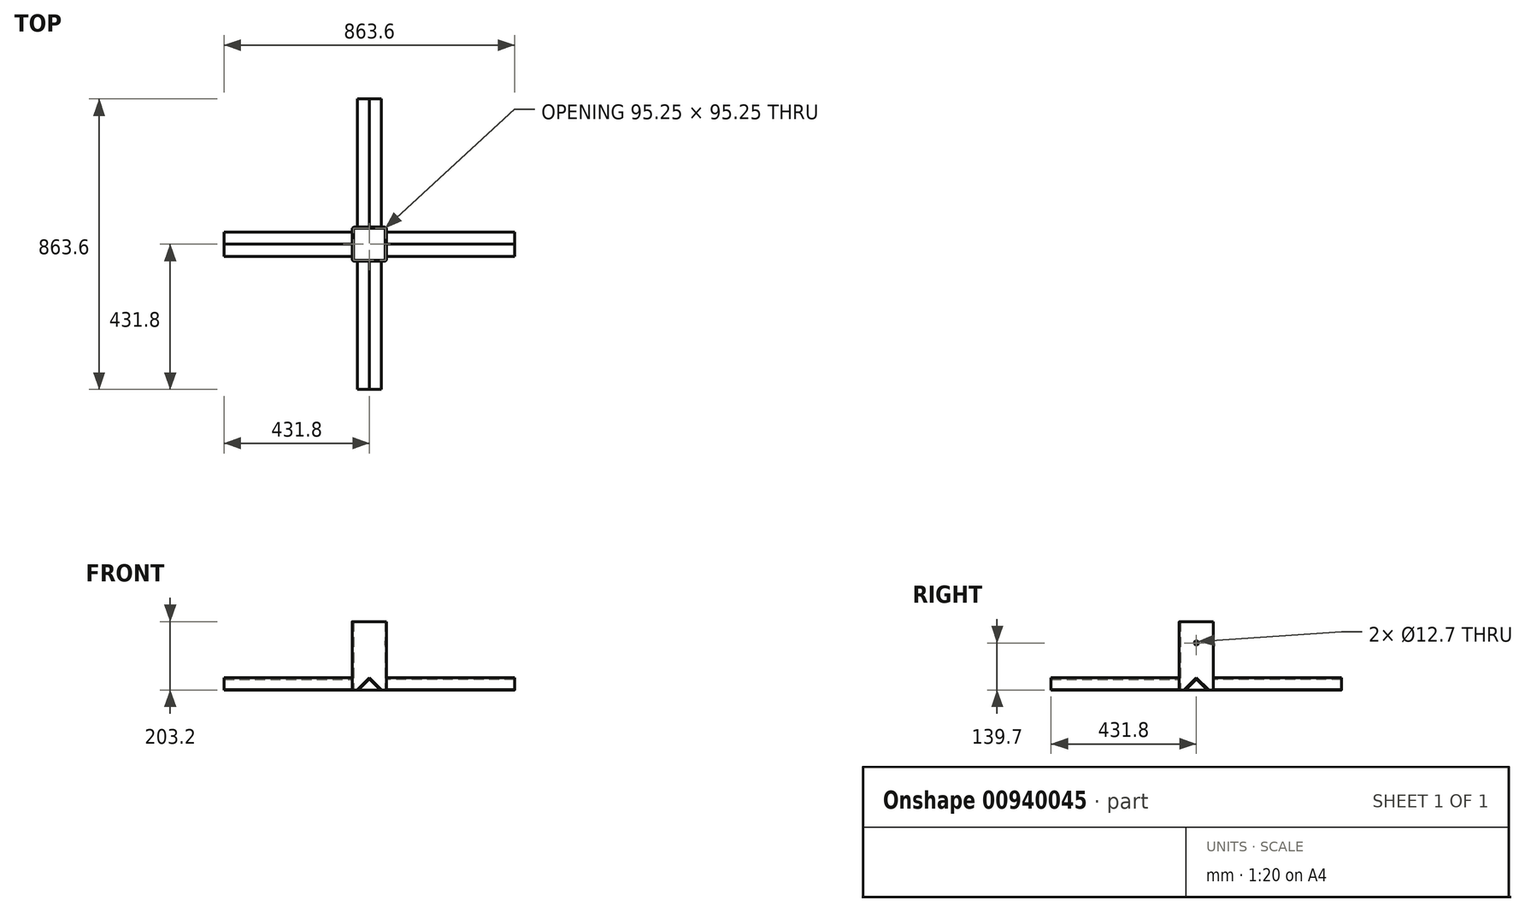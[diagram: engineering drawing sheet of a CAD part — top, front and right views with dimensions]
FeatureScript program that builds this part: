
annotation { "Feature Type Name" : "Feature", "Feature Type Description" : "" }
export const myFeature = defineFeature(function(context is Context, id is Id, definition is map)
    precondition{}
    {
        {
            var Q0;
            Q0=qCreatedBy(makeId("Top.planeOp"),FACE);
            var sketch = newSketch(context, id + "F0", { "sketchPlane" : qUnion([Q0])});
            skLineSegment(sketch, "E0.bottom", {"start": v(44.45, 50.8) * mm, "end": v(-44.45, 50.8) * mm});
            skLineSegment(sketch, "E0.top", {"start": v(44.45, -50.8) * mm, "end": v(-44.45, -50.8) * mm});
            skLineSegment(sketch, "E0.left", {"start": v(50.8, 44.45) * mm, "end": v(50.8, -44.45) * mm});
            skLineSegment(sketch, "E0.right", {"start": v(-50.8, 44.45) * mm, "end": v(-50.8, -44.45) * mm});
            skPoint(sketch, "E0.middle", {"position": v(0, 0) * mm});
            skPoint(sketch, "E1.visualSharp", {"position": v(-50.8, 50.8) * mm});
            skArc(sketch, "E1.filletArc", {"start": v(-44.45, 50.8) * mm, "mid": v(-48.94, 48.94) * mm, "end": v(-50.8, 44.45) * mm});
            skPoint(sketch, "E2.visualSharp", {"position": v(50.8, 50.8) * mm});
            skArc(sketch, "E2.filletArc", {"start": v(50.8, 44.45) * mm, "mid": v(48.94, 48.94) * mm, "end": v(44.45, 50.8) * mm});
            skPoint(sketch, "E3.visualSharp", {"position": v(50.8, -50.8) * mm});
            skArc(sketch, "E3.filletArc", {"start": v(44.45, -50.8) * mm, "mid": v(48.94, -48.94) * mm, "end": v(50.8, -44.45) * mm});
            skPoint(sketch, "E4.visualSharp", {"position": v(-50.8, -50.8) * mm});
            skArc(sketch, "E4.filletArc", {"start": v(-50.8, -44.45) * mm, "mid": v(-48.94, -48.94) * mm, "end": v(-44.45, -50.8) * mm});
            skLineSegment(sketch, "E5.0", {"start": v(47.63, 44.45) * mm, "end": v(47.63, -44.45) * mm});
            skLineSegment(sketch, "E5.1", {"start": v(44.45, 47.63) * mm, "end": v(-44.45, 47.63) * mm});
            skLineSegment(sketch, "E5.2", {"start": v(-47.63, 44.45) * mm, "end": v(-47.62, -44.45) * mm});
            skLineSegment(sketch, "E5.3", {"start": v(44.45, -47.62) * mm, "end": v(-44.45, -47.62) * mm});
            skPoint(sketch, "E6.visualSharp", {"position": v(-47.63, 47.63) * mm});
            skArc(sketch, "E6.filletArc", {"start": v(-44.45, 47.63) * mm, "mid": v(-46.7, 46.7) * mm, "end": v(-47.63, 44.45) * mm});
            skPoint(sketch, "E7.visualSharp", {"position": v(-47.62, -47.62) * mm});
            skArc(sketch, "E7.filletArc", {"start": v(-47.62, -44.45) * mm, "mid": v(-46.7, -46.7) * mm, "end": v(-44.45, -47.62) * mm});
            skPoint(sketch, "E8.visualSharp", {"position": v(47.63, -47.62) * mm});
            skArc(sketch, "E8.filletArc", {"start": v(44.45, -47.62) * mm, "mid": v(46.7, -46.7) * mm, "end": v(47.63, -44.45) * mm});
            skPoint(sketch, "E9.visualSharp", {"position": v(47.63, 47.63) * mm});
            skArc(sketch, "E9.filletArc", {"start": v(47.63, 44.45) * mm, "mid": v(46.7, 46.7) * mm, "end": v(44.45, 47.63) * mm});
            skSolve(sketch);
        }
        {
            var Q0;
            Q0 = qSketchRegion(id + "F0", true);
            extrude(context, id + "F1", {"entities" : qUnion([Q0]), "depth" : 203.2 * mm, "offsetDistance" : 25.4 * mm});
        }
        {
            var Q0;
            Q0=makeQuery(id+"F1.opExtrude","SWEPT_FACE",FACE,{"disambiguationData":[OSD([sQuery(id+"F0.wireOp",EDGE,"E0.right")])]});
            var sketch = newSketch(context, id + "F2", { "sketchPlane" : qUnion([Q0])});
            skPoint(sketch, "E10", {"position": v(0, 139.7) * mm});
            skPoint(sketch, "E10.positionSnap0", {"position": v(0, 203.2) * mm});
            skSolve(sketch);
        }
        {
            var Q0;
            Q0=sQuery(id+"F2.wireOp",VERTEX,"E10");
            var Q1;
            Q1=makeQuery(id+"F1.opExtrude","SWEPT_BODY",BODY,{"disambiguationData":[OSD([sQuery(id+"F0.wireOp",EDGE,"E0.bottom"),sQuery(id+"F0.wireOp",EDGE,"E0.top"),sQuery(id+"F0.wireOp",EDGE,"E0.left"),sQuery(id+"F0.wireOp",EDGE,"E0.right"),sQuery(id+"F0.wireOp",EDGE,"E1.filletArc"),sQuery(id+"F0.wireOp",EDGE,"E2.filletArc"),sQuery(id+"F0.wireOp",EDGE,"E3.filletArc"),sQuery(id+"F0.wireOp",EDGE,"E4.filletArc"),sQuery(id+"F0.wireOp",EDGE,"E5.0"),sQuery(id+"F0.wireOp",EDGE,"E5.1"),sQuery(id+"F0.wireOp",EDGE,"E5.2"),sQuery(id+"F0.wireOp",EDGE,"E5.3"),sQuery(id+"F0.wireOp",EDGE,"E6.filletArc"),sQuery(id+"F0.wireOp",EDGE,"E7.filletArc"),sQuery(id+"F0.wireOp",EDGE,"E8.filletArc"),sQuery(id+"F0.wireOp",EDGE,"E9.filletArc")])]});
            hole(context, id + "F3", {"style" : HoleStyle.SIMPLE, "endStyle" : HoleEndStyle.THROUGH, "holeDiameter" : 12.7 * mm, "majorDiameter" : 6.35 * mm, "isTappedThrough" : true, "tappedDepth" : 12.7 * mm, "tapClearance" : 3, "locations" : qUnion([Q0]), "scope" : qUnion([Q1])});
        }
        {
            var Q0;
            Q0=makeQuery(id+"F1.opExtrude","SWEPT_FACE",FACE,{"disambiguationData":[OSD([sQuery(id+"F0.wireOp",EDGE,"E0.left")])]});
            var sketch = newSketch(context, id + "F4", { "sketchPlane" : qUnion([Q0])});
            skLineSegment(sketch, "E11", {"start": v(0, 36.85) * mm, "end": v(35.92, 0.93) * mm});
            skLineSegment(sketch, "E12", {"start": v(0, 36.85) * mm, "end": v(-35.92, 0.93) * mm});
            skLineSegment(sketch, "E13.0", {"start": v(2.25, 30.12) * mm, "end": v(31.43, 0.93) * mm});
            skLineSegment(sketch, "E13.1", {"start": v(-2.25, 30.12) * mm, "end": v(-31.43, 0.93) * mm});
            skLineSegment(sketch, "E14", {"start": v(35.92, 0.93) * mm, "end": v(35.92, 0.93) * mm});
            skLineSegment(sketch, "E15", {"start": v(-35.92, 0.93) * mm, "end": v(-35.92, 0.93) * mm});
            skPoint(sketch, "E16.visualSharp", {"position": v(33.68, -1.32) * mm});
            skArc(sketch, "E16.filletArc", {"start": v(31.43, 0.93) * mm, "mid": v(33.68, 0) * mm, "end": v(35.92, 0.93) * mm});
            skPoint(sketch, "E17.visualSharp", {"position": v(-33.68, -1.32) * mm});
            skArc(sketch, "E17.filletArc", {"start": v(-35.92, 0.93) * mm, "mid": v(-33.68, 0) * mm, "end": v(-31.43, 0.93) * mm});
            skPoint(sketch, "E18.visualSharp", {"position": v(-2.06, 30.3) * mm});
            skArc(sketch, "E19", {"start": v(2.25, 30.12) * mm, "mid": v(0, 31.05) * mm, "end": v(-2.25, 30.12) * mm});
            skSolve(sketch);
        }
        {
            var Q0;
            Q0=makeQuery(id+"F1.opExtrude","SWEPT_FACE",FACE,{"disambiguationData":[OSD([sQuery(id+"F0.wireOp",EDGE,"E0.bottom")])]});
            var sketch = newSketch(context, id + "F5", { "sketchPlane" : qUnion([Q0])});
            skLineSegment(sketch, "E20", {"start": v(0, 36.85) * mm, "end": v(35.92, 0.93) * mm});
            skLineSegment(sketch, "E21", {"start": v(0, 36.85) * mm, "end": v(-35.92, 0.93) * mm});
            skLineSegment(sketch, "E22.0", {"start": v(2.25, 30.12) * mm, "end": v(31.43, 0.93) * mm});
            skLineSegment(sketch, "E22.1", {"start": v(-2.25, 30.12) * mm, "end": v(-31.43, 0.93) * mm});
            skLineSegment(sketch, "E23", {"start": v(35.92, 0.93) * mm, "end": v(35.92, 0.93) * mm});
            skLineSegment(sketch, "E24", {"start": v(-35.92, 0.93) * mm, "end": v(-35.92, 0.93) * mm});
            skPoint(sketch, "E25.visualSharp", {"position": v(33.68, -1.32) * mm});
            skArc(sketch, "E25.filletArc", {"start": v(31.43, 0.93) * mm, "mid": v(33.68, 0) * mm, "end": v(35.92, 0.93) * mm});
            skPoint(sketch, "E26.visualSharp", {"position": v(-33.68, -1.32) * mm});
            skArc(sketch, "E26.filletArc", {"start": v(-35.92, 0.93) * mm, "mid": v(-33.68, 0) * mm, "end": v(-31.43, 0.93) * mm});
            skPoint(sketch, "E27.visualSharp", {"position": v(10.04, 42.4) * mm});
            skArc(sketch, "E28", {"start": v(2.25, 30.12) * mm, "mid": v(0, 31.05) * mm, "end": v(-2.25, 30.12) * mm});
            skLineSegment(sketch, "E29", {"start": v(0, 0) * mm, "end": v(0, 53.54) * mm, "construction": true});
            skSolve(sketch);
        }
        {
            var Q0;
            Q0=makeQuery(id+"F1.opExtrude","SWEPT_FACE",FACE,{"disambiguationData":[OSD([sQuery(id+"F0.wireOp",EDGE,"E0.right")])]});
            var sketch = newSketch(context, id + "F6", { "sketchPlane" : qUnion([Q0])});
            skLineSegment(sketch, "E30.0", {"start": v(-2.25, 30.12) * mm, "end": v(-31.43, 0.93) * mm});
            skLineSegment(sketch, "E30.1", {"start": v(0, 36.85) * mm, "end": v(-35.92, 0.93) * mm});
            skLineSegment(sketch, "E30.2", {"start": v(2.25, 30.12) * mm, "end": v(31.43, 0.93) * mm});
            skLineSegment(sketch, "E30.3", {"start": v(0, 36.85) * mm, "end": v(35.92, 0.93) * mm});
            skArc(sketch, "E30.4", {"start": v(-2.25, 30.12) * mm, "mid": v(0, 31.05) * mm, "end": v(2.25, 30.12) * mm});
            skArc(sketch, "E30.5", {"start": v(-31.43, 0.93) * mm, "mid": v(-33.68, 0) * mm, "end": v(-35.92, 0.93) * mm});
            skArc(sketch, "E30.6", {"start": v(35.92, 0.93) * mm, "mid": v(33.68, 0) * mm, "end": v(31.43, 0.93) * mm});
            skSolve(sketch);
        }
        {
            var Q0;
            Q0=makeQuery(id+"F1.opExtrude","SWEPT_FACE",FACE,{"disambiguationData":[OSD([sQuery(id+"F0.wireOp",EDGE,"E0.top")])]});
            var sketch = newSketch(context, id + "F7", { "sketchPlane" : qUnion([Q0])});
            skLineSegment(sketch, "E31.0", {"start": v(-2.25, 30.12) * mm, "end": v(-31.43, 0.93) * mm});
            skLineSegment(sketch, "E31.1", {"start": v(0, 36.85) * mm, "end": v(-35.92, 0.93) * mm});
            skArc(sketch, "E31.2", {"start": v(-31.43, 0.93) * mm, "mid": v(-33.68, 0) * mm, "end": v(-35.92, 0.93) * mm});
            skLineSegment(sketch, "E31.3", {"start": v(2.25, 30.12) * mm, "end": v(31.43, 0.93) * mm});
            skLineSegment(sketch, "E31.4", {"start": v(0, 36.85) * mm, "end": v(35.92, 0.93) * mm});
            skArc(sketch, "E31.5", {"start": v(-2.25, 30.12) * mm, "mid": v(0, 31.05) * mm, "end": v(2.25, 30.12) * mm});
            skArc(sketch, "E31.6", {"start": v(35.92, 0.93) * mm, "mid": v(33.68, 0) * mm, "end": v(31.43, 0.93) * mm});
            skSolve(sketch);
        }
        {
            var Q0;
            Q0 = qSketchRegion(id + "F7", true);
            extrude(context, id + "F8", {"entities" : qUnion([Q0]), "operationType" : NewBodyOperationType.ADD, "depth" : 381 * mm, "offsetDistance" : 25.4 * mm});
        }
        {
            var Q0;
            {var subQ3=sQuery(id+"F4.wireOp",EDGE,"E11");Q0=makeQuery(id+"F4.imprint","IMPRINT",FACE,{"disambiguationData":[TD([[makeQuery(id+"F4.imprint","IMPRINT",EDGE,{"derivedFrom":subQ3}),-1.0]])]});}
            extrude(context, id + "F9", {"entities" : qUnion([Q0]), "operationType" : NewBodyOperationType.ADD, "depth" : 381 * mm, "offsetDistance" : 25.4 * mm});
        }
        {
            var Q0;
            {var subQ3=sQuery(id+"F5.wireOp",EDGE,"E20");Q0=makeQuery(id+"F5.imprint","IMPRINT",FACE,{"disambiguationData":[TD([[makeQuery(id+"F5.imprint","IMPRINT",EDGE,{"derivedFrom":subQ3}),-1.0]])]});}
            extrude(context, id + "F10", {"entities" : qUnion([Q0]), "operationType" : NewBodyOperationType.ADD, "depth" : 381 * mm, "offsetDistance" : 25.4 * mm});
        }
        {
            var Q0;
            {var subQ3=sQuery(id+"F6.wireOp",EDGE,"E30.0");Q0=makeQuery(id+"F6.imprint","IMPRINT",FACE,{"disambiguationData":[TD([[makeQuery(id+"F6.imprint","IMPRINT",EDGE,{"derivedFrom":subQ3}),-1.0]])]});}
            extrude(context, id + "F11", {"entities" : qUnion([Q0]), "operationType" : NewBodyOperationType.ADD, "depth" : 381 * mm, "offsetDistance" : 25.4 * mm});
        }
    });
